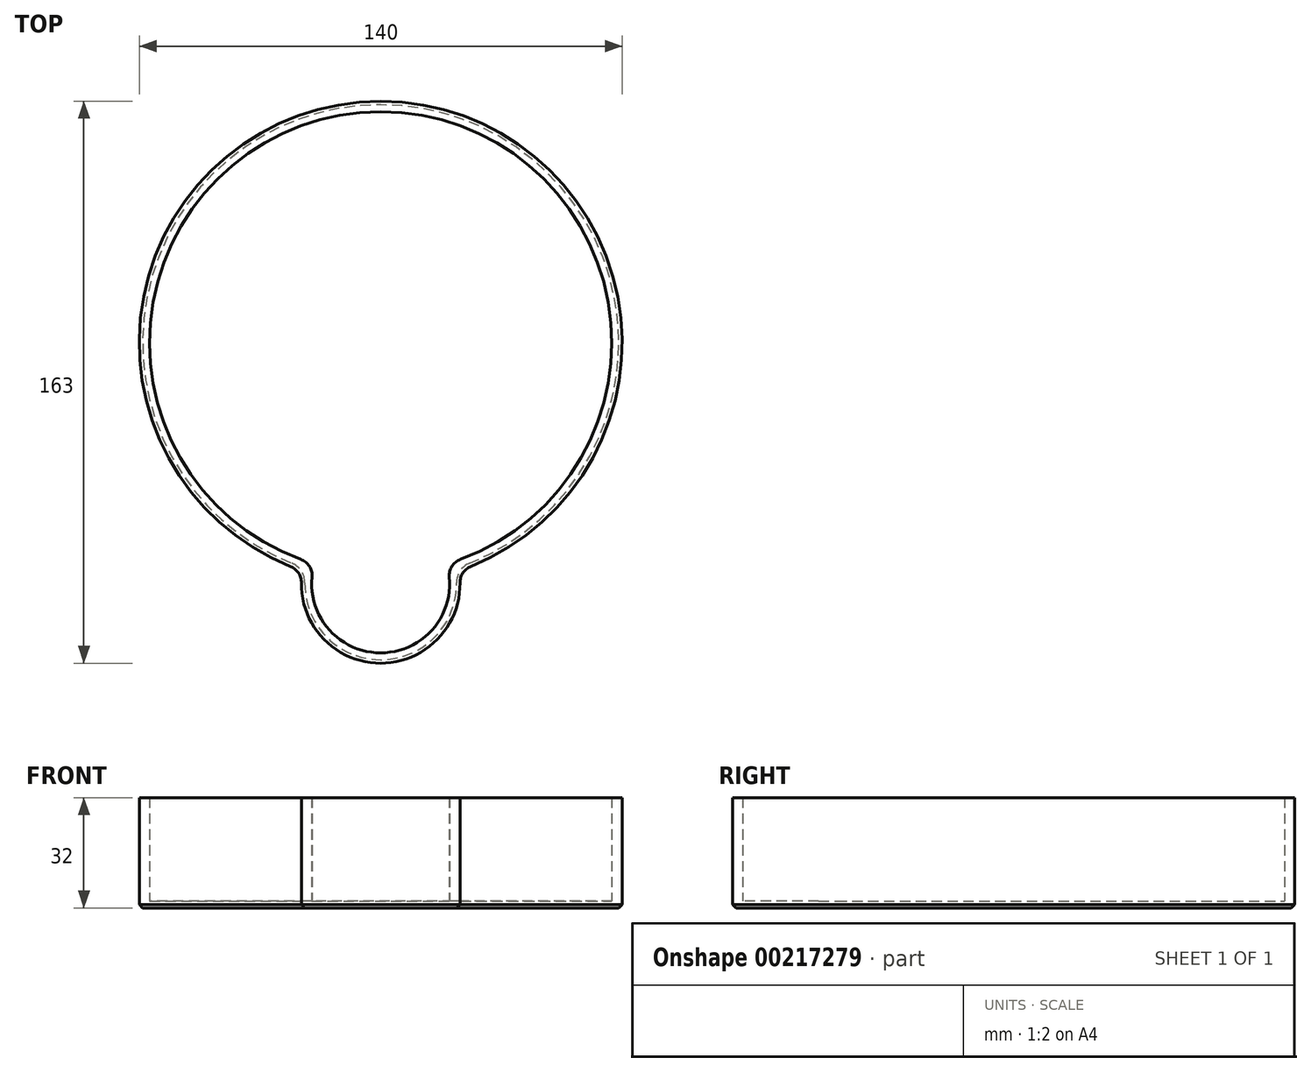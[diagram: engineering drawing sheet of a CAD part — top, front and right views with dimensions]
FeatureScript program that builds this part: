
annotation { "Feature Type Name" : "Feature", "Feature Type Description" : "" }
export const myFeature = defineFeature(function(context is Context, id is Id, definition is map)
    precondition{}
    {
        {
            var Q0;
            Q0=qCreatedBy(makeId("Top.planeOp"),FACE);
            var sketch = newSketch(context, id + "F0", { "sketchPlane" : qUnion([Q0])});
            skArc(sketch, "E0", {"start": v(26.13, -64.94) * mm, "mid": v(0, 70) * mm, "end": v(-26.13, -64.94) * mm});
            skArc(sketch, "E1", {"start": v(23.15, -62.87) * mm, "mid": v(0, 67) * mm, "end": v(-23.15, -62.87) * mm});
            skArc(sketch, "E2", {"start": v(-23, -69.65) * mm, "mid": v(0, -93) * mm, "end": v(23, -69.65) * mm});
            skArc(sketch, "E3", {"start": v(-19.9, -68.05) * mm, "mid": v(0, -90) * mm, "end": v(19.9, -68.05) * mm});
            skPoint(sketch, "E4.visualSharp", {"position": v(22.69, -66.22) * mm});
            skArc(sketch, "E4.filletArc", {"start": v(26.13, -64.94) * mm, "mid": v(23.83, -66.81) * mm, "end": v(23, -69.65) * mm});
            skPoint(sketch, "E5.visualSharp", {"position": v(-22.69, -66.22) * mm});
            skArc(sketch, "E5.filletArc", {"start": v(-23, -69.65) * mm, "mid": v(-23.83, -66.81) * mm, "end": v(-26.13, -64.94) * mm});
            skPoint(sketch, "E6.visualSharp", {"position": v(-19.14, -64.2) * mm});
            skArc(sketch, "E6.filletArc", {"start": v(-19.9, -68.05) * mm, "mid": v(-20.65, -64.9) * mm, "end": v(-23.15, -62.87) * mm});
            skPoint(sketch, "E7.visualSharp", {"position": v(19.14, -64.2) * mm});
            skArc(sketch, "E7.filletArc", {"start": v(23.15, -62.87) * mm, "mid": v(20.65, -64.9) * mm, "end": v(19.9, -68.05) * mm});
            skSolve(sketch);
        }
        {
            var Q0;
            Q0=qSketchRegion(id+"F0",true);
            extrude(context, id + "F1", {"entities" : qUnion([Q0]), "offsetDistance" : 25 * mm, "depth" : 30 * mm});
        }
        {
            var Q0;
            Q0=qCreatedBy(makeId("Top.planeOp"),FACE);
            var sketch = newSketch(context, id + "F2", { "sketchPlane" : qUnion([Q0])});
            skArc(sketch, "E8", {"start": v(26.13, -64.94) * mm, "mid": v(0, 70) * mm, "end": v(-26.13, -64.94) * mm});
            skArc(sketch, "E9.0", {"start": v(-23, -69.65) * mm, "mid": v(0, -93) * mm, "end": v(23, -69.65) * mm});
            skArc(sketch, "E9.1", {"start": v(-23, -69.65) * mm, "mid": v(-23.83, -66.81) * mm, "end": v(-26.13, -64.94) * mm});
            skArc(sketch, "E9.2", {"start": v(26.13, -64.94) * mm, "mid": v(23.83, -66.81) * mm, "end": v(23, -69.65) * mm});
            skSolve(sketch);
        }
        {
            var Q0;
            Q0=qSketchRegion(id+"F2",true);
            extrude(context, id + "F3", {"entities" : qUnion([Q0]), "operationType" : NewBodyOperationType.ADD, "oppositeDirection" : true, "offsetDistance" : 25 * mm, "depth" : 2 * mm});
        }
        {
            var Q0;
            Q0=makeQuery(id+"F3.opExtrude","CAP_EDGE",EDGE,{"disambiguationData":[OSD([sQuery(id+"F2.wireOp",EDGE,"E8")])],"isStart":false});
            chamfer(context, id + "F4", {"entities" : qUnion([Q0]), "width" : 1 * mm, "tangentPropagation" : true});
        }
    });
